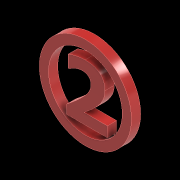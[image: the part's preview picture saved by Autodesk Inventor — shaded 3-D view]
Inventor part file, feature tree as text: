
AUTODESK INVENTOR PART (.ipt)
format: ipt  version: 2020 (Build 240168000, 168)  size: 157,184 bytes
history: native  units: mm
features: other x5, extrude x2, sketch x2
ambient origin geometry x8: Origin, YZ Plane, XZ Plane, XY Plane, X Axis, Y Axis, Z Axis, Center Point
bodies: Body1 (feature_tree)
feature tree (9):
  other  "自動販賣機.ipt"
  extrude  "擠出1"  Depth=10.0mm
  extrude  "擠出2"  Depth=10.0mm TaperAngle=0.0deg
  other  "實體49::自動販賣機.ipt"
  other  "標籤特徵1"
  sketch  "草圖1"
  sketch  "草圖2"
  other  "實體1"
  other  "投影切割邊1"
